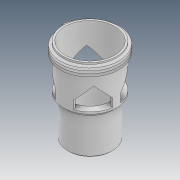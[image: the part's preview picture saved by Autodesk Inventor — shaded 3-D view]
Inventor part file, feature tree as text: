
AUTODESK INVENTOR PART (.ipt)
format: ipt  version: 2020 (Build 240168000, 168)  size: 305,152 bytes
history: native  units: mm
features: sketch x5, chamfer x4, extrude x3, revolve x1, plane x1, helix x1
ambient origin geometry x8: Origin, YZ Plane, XZ Plane, XY Plane, X Axis, Y Axis, Z Axis, Center Point
bodies: Solid1 (feature_tree)
feature tree (15):
  revolve  "Revolution1"  [1 undecoded]
  chamfer  "Chamfer1"  Distance=0.6mm Angle=45.0deg
  extrude  "Extrusion1"  Depth=26.4mm
  chamfer  "Chamfer2"  Distance=1.0mm
  extrude  "Extrusion2"  Depth=2.0mm TaperAngle=45.0deg
  extrude  "Extrusion3"  Depth=24.5mm
  chamfer  "Chamfer3"  Distance=9.0mm
  sketch  "Sketch5"  dims[d9=9.8mm d10=26.4mm d11=1.0mm d12=0.0mm d13=2.0mm d14=2.0mm d15=45.0deg d16=24.5mm d17=9.0mm d18=4.0mm d19=11.0mm d20=0.0mm d21=10.0mm d22=0.0mm d23=6.73mm d24=2.0mm d25=45.0deg d27=1.25mm d36=-0.625mm d55=1.25mm d56=1.25mm d57=5.0mm d58=10.0mm d59=0.0mm d60=90.0deg d61=90.0deg d62=0.0mm d63=0.0mm d64=0.559mm d65=2.0mm d66=45.0deg]
  plane  "Work Plane1"
  helix  "Coil3"  [1 undecoded]
  chamfer  "Chamfer5"  Distance=11.0mm
  sketch  "Sketch1"  dims[d0=20.0mm d1=11.2mm]
  sketch  "Sketch2"  dims[d2=11.0mm]
  sketch  "Sketch3"  dims[d4=180.0deg]
  sketch  "Sketch4"  dims[d5=90.0deg d6=0.6mm d7=2.0mm d8=45.0deg]
note: 2 required parameter values undecoded (feature->parameter linkage not recoverable at this tier; creation-order binding heuristic only, values carry confidence <= 0.55)